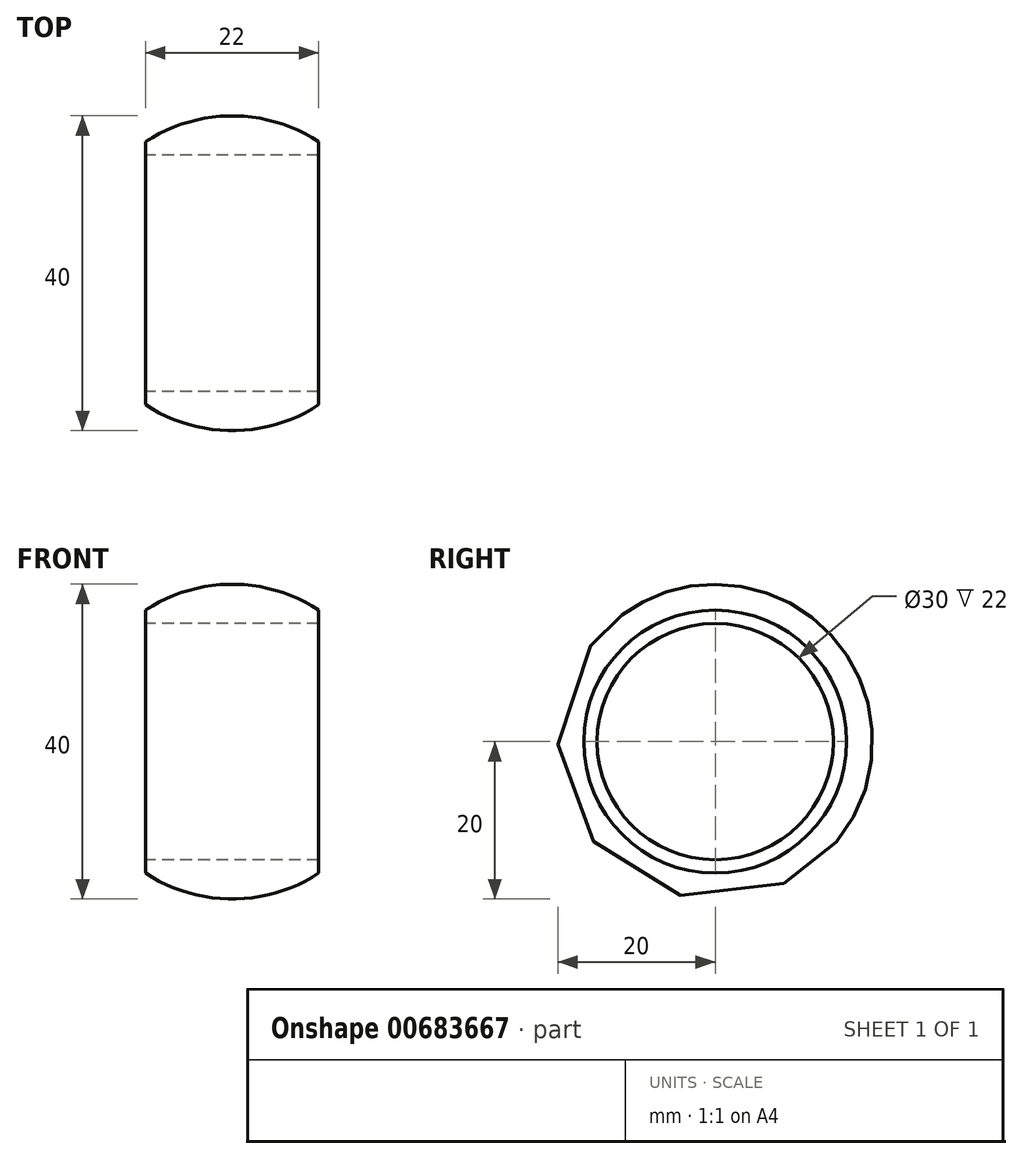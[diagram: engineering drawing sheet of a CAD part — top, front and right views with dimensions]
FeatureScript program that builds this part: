
annotation { "Feature Type Name" : "Feature", "Feature Type Description" : "" }
export const myFeature = defineFeature(function(context is Context, id is Id, definition is map)
    precondition{}
    {
        {
            var Q0;
            Q0=qCreatedBy(makeId("Front.planeOp"),FACE);
            var sketch = newSketch(context, id + "F0", { "sketchPlane" : qUnion([Q0])});
            skLineSegment(sketch, "E0", {"start": v(0, 0) * mm, "end": v(91.76, 0) * mm, "construction": true});
            skLineSegment(sketch, "E1", {"start": v(0, 15) * mm, "end": v(22, 15) * mm});
            skLineSegment(sketch, "E2", {"start": v(0, 15) * mm, "end": v(0, 16.7) * mm});
            skLineSegment(sketch, "E3", {"start": v(22, 15) * mm, "end": v(22, 16.7) * mm});
            skArc(sketch, "E4", {"start": v(22, 16.7) * mm, "mid": v(11, 20) * mm, "end": v(0, 16.7) * mm});
            skSolve(sketch);
        }
        {
            var Q0;
            Q0=makeQuery(id+"F0.imprint","IMPRINT",FACE,{"disambiguationData":[TD([[makeQuery(id+"F0.imprint","IMPRINT",EDGE,{"derivedFrom":sQuery(id+"F0.wireOp",EDGE,"E1")}),1.0]])]});
            var Q1;
            Q1=sQuery(id+"F0.wireOp",EDGE,"E0");
            revolve(context, id + "F1", {"entities" : qUnion([Q0]), "axis" : qUnion([Q1]), "revolveType" : RevolveType.FULL});
        }
    });
